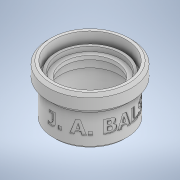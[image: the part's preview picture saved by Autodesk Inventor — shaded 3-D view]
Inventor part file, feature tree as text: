
AUTODESK INVENTOR PART (.ipt)
format: ipt  version: 2021 (Build 250183000, 183)  size: 525,824 bytes
history: native  units: mm
features: sketch x7, extrude x6, chamfer x3, emboss x1
ambient origin geometry x8: Origin, YZ Plane, XZ Plane, XY Plane, X Axis, Y Axis, Z Axis, Center Point
bodies: Solid1 (feature_tree)
feature tree (17):
  extrude  "Extrusion1"  Depth=3.0mm
  extrude  "Extrusion2"  Depth=39.0mm
  chamfer  "Chamfer1"  Distance=7.5mm
  extrude  "Extrusion3"  Depth=28.0mm
  extrude  "Extrusion4"  Depth=31.4mm
  extrude  "Extrusion5"  Depth=1.5mm
  chamfer  "Chamfer2"  Distance=5.0mm
  extrude  "Extrusion6"  Depth=1.5mm TaperAngle=45.0deg
  chamfer  "Chamfer3"  Distance=5.0mm
  emboss  "Emboss1"
  sketch  "Sketch1"  dims[d0=33.6mm d1=3.0mm]
  sketch  "Sketch2"  dims[d2=20.0mm d3=0.0mm d4=39.0mm]
  sketch  "Sketch3"  dims[d5=3.0mm d6=7.5mm d7=0.0mm]
  sketch  "Sketch4"  dims[d8=2.7mm d9=2.0mm d10=45.0deg d11=28.0mm]
  sketch  "Sketch5"  dims[d12=2.0mm d13=0.0mm d14=31.4mm]
  sketch  "Sketch6"  dims[d15=5.0mm d16=0.0mm d17=1.5mm]
  sketch  "Sketch7"  dims[d18=3.0mm d19=5.0mm d20=0.0mm d21=1.5mm d22=2.0mm d23=45.0deg d24=5.0mm d25=0.0mm d26=1.5mm d27=2.0mm d28=45.0deg d29=0.5mm d30=0.0mm]
